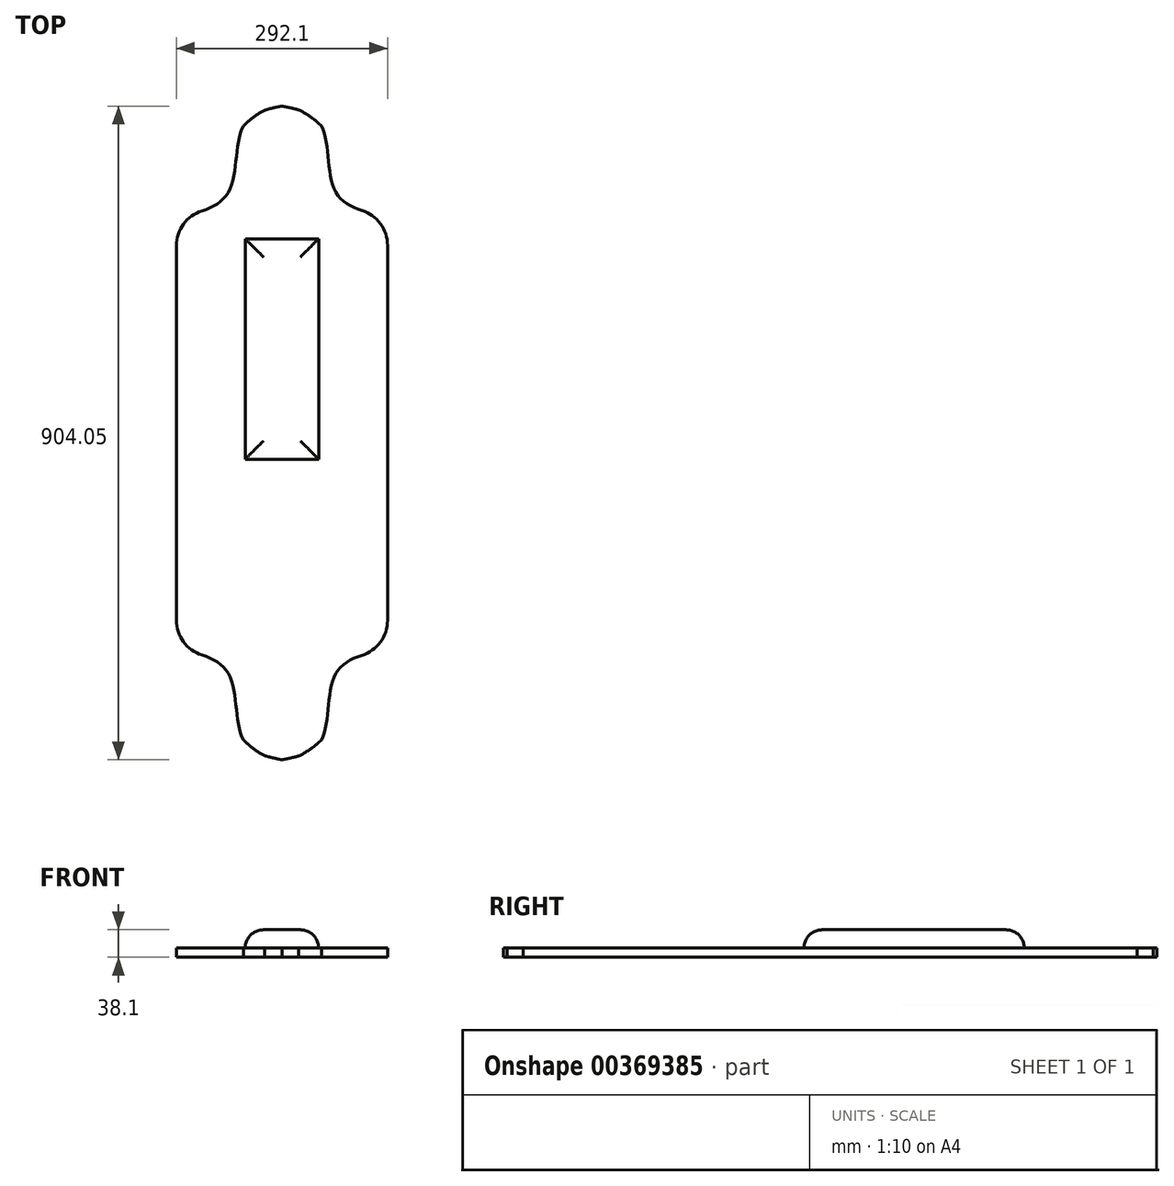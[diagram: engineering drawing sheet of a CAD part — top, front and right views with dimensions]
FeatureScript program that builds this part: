
annotation { "Feature Type Name" : "Feature", "Feature Type Description" : "" }
export const myFeature = defineFeature(function(context is Context, id is Id, definition is map)
    precondition{}
    {
        {
            var Q0;
            Q0=qCreatedBy(makeId("Top.planeOp"),FACE);
            var sketch = newSketch(context, id + "F0", { "sketchPlane" : qUnion([Q0])});
            skLineSegment(sketch, "E0", {"start": v(-146.05, 268.28) * mm, "end": v(-146.05, 9.59) * mm});
            skLineSegment(sketch, "E1", {"start": v(146.05, 268.76) * mm, "end": v(146.05, 9.59) * mm});
            skPoint(sketch, "E2", {"position": v(0, 309.21) * mm});
            skPoint(sketch, "E3", {"position": v(0, 461.61) * mm});
            skFitSpline(sketch, "E4", {"points": [v(-146.05, 309.21) * mm, v(0, 461.61) * mm, v(146.05, 309.21) * mm], "startDerivative": vector(304.65, 455.86) * mm, "endDerivative": vector(279.48, -458.61) * mm});
            skFitSpline(sketch, "E5", {"points": [v(-146.05, 309.21) * mm, v(-74.15, 342.44) * mm, v(-53.33, 434.23) * mm, v(0, 461.61) * mm], "startDerivative": vector(263.83, 40.94) * mm, "endDerivative": vector(221.42, 45.73) * mm});
            skLineSegment(sketch, "E6", {"start": v(-74.15, 342.44) * mm, "end": v(0, 342.44) * mm, "construction": true});
            skLineSegment(sketch, "E7", {"start": v(0, 342.44) * mm, "end": v(74.53, 342.44) * mm, "construction": true});
            skLineSegment(sketch, "E8", {"start": v(74.53, 342.44) * mm, "end": v(77.26, 325.62) * mm, "construction": true});
            skLineSegment(sketch, "E9", {"start": v(-53.33, 434.23) * mm, "end": v(54.65, 434.23) * mm, "construction": true});
            skLineSegment(sketch, "E10", {"start": v(0, 342.44) * mm, "end": v(0, 309.21) * mm, "construction": true});
            skLineSegment(sketch, "E11", {"start": v(-146.05, 309.21) * mm, "end": v(-74.15, 309.21) * mm, "construction": true});
            skLineSegment(sketch, "E12", {"start": v(-74.15, 309.21) * mm, "end": v(-74.15, 9.59) * mm, "construction": true});
            skLineSegment(sketch, "E13", {"start": v(0, 434.23) * mm, "end": v(0, 309.21) * mm, "construction": true});
            skLineSegment(sketch, "E14", {"start": v(-53.33, 434.23) * mm, "end": v(0, 434.23) * mm, "construction": true});
            skLineSegment(sketch, "E15", {"start": v(54.65, 434.23) * mm, "end": v(54.65, 9.59) * mm, "construction": true});
            skFitSpline(sketch, "E16", {"points": [v(146.05, 309.21) * mm, v(74.53, 342.44) * mm, v(54.65, 434.23) * mm, v(0, 461.61) * mm], "startDerivative": vector(-262.66, 48.53) * mm, "endDerivative": vector(-225.77, 45.03) * mm});
            skLineSegment(sketch, "E17", {"start": v(74.53, 342.44) * mm, "end": v(74.53, 9.59) * mm, "construction": true});
            skArc(sketch, "E18.filletArc", {"start": v(-110.48, 316.74) * mm, "mid": v(-136.2, 298.33) * mm, "end": v(-146.05, 268.28) * mm});
            skArc(sketch, "E19.filletArc", {"start": v(146.05, 268.76) * mm, "mid": v(136.21, 298.8) * mm, "end": v(110.52, 317.22) * mm});
            skLineSegment(sketch, "E20.0", {"start": v(-146.05, 9.59) * mm, "end": v(146.05, 9.59) * mm, "construction": true});
            skLineSegment(sketch, "E21.MirrorCS", {"start": v(0, -323.26) * mm, "end": v(0, -290.04) * mm, "construction": true});
            skPoint(sketch, "E22.MirrorP", {"position": v(0, -290.04) * mm});
            skArc(sketch, "E23.MirrorCS", {"start": v(-110.48, -297.56) * mm, "mid": v(-136.2, -279.16) * mm, "end": v(-146.05, -249.1) * mm});
            skPoint(sketch, "E24.MirrorP", {"position": v(146.05, -290.04) * mm});
            skPoint(sketch, "E25.MirrorP", {"position": v(0, -442.44) * mm});
            skFitSpline(sketch, "E26.MirrorCS", {"points": [v(-146.05, -290.04) * mm, v(0, -442.44) * mm, v(146.05, -290.04) * mm], "startDerivative": vector(304.65, -455.86) * mm, "endDerivative": vector(279.48, 458.61) * mm});
            skLineSegment(sketch, "E27.MirrorCS", {"start": v(0, -323.26) * mm, "end": v(74.53, -323.26) * mm, "construction": true});
            skArc(sketch, "E28.MirrorCS", {"start": v(146.05, -249.59) * mm, "mid": v(136.21, -279.63) * mm, "end": v(110.52, -298.04) * mm});
            skFitSpline(sketch, "E29.MirrorCS", {"points": [v(146.05, -290.04) * mm, v(74.53, -323.26) * mm, v(54.65, -415.05) * mm, v(0, -442.44) * mm], "startDerivative": vector(-262.66, -48.53) * mm, "endDerivative": vector(-225.77, -45.03) * mm});
            skFitSpline(sketch, "E30.MirrorCS", {"points": [v(-146.05, -290.04) * mm, v(-74.15, -323.26) * mm, v(-53.33, -415.05) * mm, v(0, -442.44) * mm], "startDerivative": vector(263.83, -40.94) * mm, "endDerivative": vector(221.42, -45.73) * mm});
            skLineSegment(sketch, "E31.MirrorCS", {"start": v(-146.05, -290.04) * mm, "end": v(-74.15, -290.04) * mm, "construction": true});
            skLineSegment(sketch, "E32.MirrorCS", {"start": v(-53.33, -415.05) * mm, "end": v(0, -415.05) * mm, "construction": true});
            skLineSegment(sketch, "E33.MirrorCS", {"start": v(-53.33, -415.05) * mm, "end": v(54.65, -415.05) * mm, "construction": true});
            skLineSegment(sketch, "E34.MirrorCS", {"start": v(74.53, -323.26) * mm, "end": v(77.26, -306.44) * mm, "construction": true});
            skLineSegment(sketch, "E35.MirrorCS", {"start": v(-74.15, -323.26) * mm, "end": v(0, -323.26) * mm, "construction": true});
            skLineSegment(sketch, "E36.MirrorCS", {"start": v(0, -415.05) * mm, "end": v(0, -290.04) * mm, "construction": true});
            skLineSegment(sketch, "E37.MirrorCS", {"start": v(74.53, -323.26) * mm, "end": v(74.53, 9.59) * mm, "construction": true});
            skLineSegment(sketch, "E38.MirrorCS", {"start": v(-146.05, -249.1) * mm, "end": v(-146.05, 9.59) * mm});
            skFitSpline(sketch, "E39.MirrorCS", {"points": [v(146.05, -290.04) * mm, v(74.53, -323.26) * mm, v(54.65, -415.05) * mm, v(0, -442.44) * mm], "startDerivative": vector(-262.66, -48.53) * mm, "endDerivative": vector(-225.77, -45.03) * mm});
            skLineSegment(sketch, "E40.MirrorCS", {"start": v(54.65, -415.05) * mm, "end": v(54.65, 9.59) * mm, "construction": true});
            skLineSegment(sketch, "E41.MirrorCS", {"start": v(146.05, -249.59) * mm, "end": v(146.05, 9.59) * mm});
            skLineSegment(sketch, "E42.MirrorCS", {"start": v(-74.15, -290.04) * mm, "end": v(-74.15, 9.59) * mm, "construction": true});
            skSolve(sketch);
        }
        {
            var Q0;
            Q0=makeQuery(id+"F0.imprint","IMPRINT",FACE,{"disambiguationData":[TD([[makeQuery(id+"F0.imprint","IMPRINT",EDGE,{"derivedFrom":sQuery(id+"F0.wireOp",EDGE,"E0")}),1.0]])]});
            extrude(context, id + "F1", {"entities" : qUnion([Q0]), "depth" : 12.7 * mm});
        }
        {
            var Q0;
            Q0=makeQuery(id+"F1.opExtrude","CAP_FACE",FACE,{"disambiguationData":[OSD([sQuery(id+"F0.wireOp",EDGE,"E0"),sQuery(id+"F0.wireOp",EDGE,"E1"),sQuery(id+"F0.wireOp",EDGE,"E4"),sQuery(id+"F0.wireOp",EDGE,"E5"),sQuery(id+"F0.wireOp",EDGE,"E16"),sQuery(id+"F0.wireOp",EDGE,"E18.filletArc"),sQuery(id+"F0.wireOp",EDGE,"E19.filletArc"),sQuery(id+"F0.wireOp",EDGE,"E38.MirrorCS"),sQuery(id+"F0.wireOp",EDGE,"E26.MirrorCS"),sQuery(id+"F0.wireOp",EDGE,"E23.MirrorCS"),sQuery(id+"F0.wireOp",EDGE,"E39.MirrorCS"),sQuery(id+"F0.wireOp",EDGE,"E41.MirrorCS"),sQuery(id+"F0.wireOp",EDGE,"E28.MirrorCS"),sQuery(id+"F0.wireOp",EDGE,"E30.MirrorCS")])],"isStart":false});
            var sketch = newSketch(context, id + "F2", { "sketchPlane" : qUnion([Q0])});
            skLineSegment(sketch, "E43.bottom", {"start": v(50.8, -26.67) * mm, "end": v(-50.8, -26.67) * mm});
            skLineSegment(sketch, "E43.top", {"start": v(50.8, 278.13) * mm, "end": v(-50.8, 278.13) * mm});
            skLineSegment(sketch, "E43.left", {"start": v(50.8, -26.67) * mm, "end": v(50.8, 278.13) * mm});
            skLineSegment(sketch, "E43.right", {"start": v(-50.8, -26.67) * mm, "end": v(-50.8, 278.13) * mm});
            skPoint(sketch, "E43.middle", {"position": v(0, 125.73) * mm});
            skLineSegment(sketch, "E44.0", {"start": v(63.5, 290.83) * mm, "end": v(-63.5, 290.83) * mm});
            skLineSegment(sketch, "E44.1", {"start": v(63.5, -39.37) * mm, "end": v(63.5, 290.83) * mm});
            skLineSegment(sketch, "E44.2", {"start": v(63.5, -39.37) * mm, "end": v(-63.5, -39.37) * mm});
            skLineSegment(sketch, "E44.3", {"start": v(-63.5, -39.37) * mm, "end": v(-63.5, 290.83) * mm});
            skLineSegment(sketch, "E45", {"start": v(-63.5, -39.37) * mm, "end": v(-50.8, -26.67) * mm});
            skLineSegment(sketch, "E46", {"start": v(63.5, -39.37) * mm, "end": v(50.8, -26.67) * mm});
            skLineSegment(sketch, "E47", {"start": v(-63.5, 290.83) * mm, "end": v(-50.8, 278.13) * mm});
            skLineSegment(sketch, "E48", {"start": v(63.5, 290.83) * mm, "end": v(50.8, 278.13) * mm});
            skSolve(sketch);
        }
        {
            var Q0;
            Q0=makeQuery(id+"F2.imprint","IMPRINT",FACE,{"disambiguationData":[TD([[makeQuery(id+"F2.imprint","IMPRINT",EDGE,{"derivedFrom":sQuery(id+"F2.wireOp",EDGE,"E43.bottom")}),-1.0]])]});
            extrude(context, id + "F3", {"entities" : qUnion([Q0]), "operationType" : NewBodyOperationType.ADD, "depth" : 25.4 * mm});
        }
        {
            var Q0;
            Q0=makeQuery(id+"F3.opExtrude","CAP_EDGE",EDGE,{"disambiguationData":[OSD([sQuery(id+"F2.wireOp",EDGE,"E43.left")])],"isStart":false});
            var Q1;
            Q1=makeQuery(id+"F3.opExtrude","CAP_EDGE",EDGE,{"disambiguationData":[OSD([sQuery(id+"F2.wireOp",EDGE,"E43.bottom")])],"isStart":false});
            var Q2;
            Q2=makeQuery(id+"F3.opExtrude","CAP_EDGE",EDGE,{"disambiguationData":[OSD([sQuery(id+"F2.wireOp",EDGE,"E43.right")])],"isStart":false});
            var Q3;
            Q3=makeQuery(id+"F3.opExtrude","CAP_EDGE",EDGE,{"disambiguationData":[OSD([sQuery(id+"F2.wireOp",EDGE,"E43.top")])],"isStart":false});
            fillet(context, id + "F4", {"entities" : qUnion([Q0, Q1, Q2, Q3]), "radius" : 25.4 * mm, "tangentPropagation" : true, "allowEdgeOverflow" : false});
        }
    });
